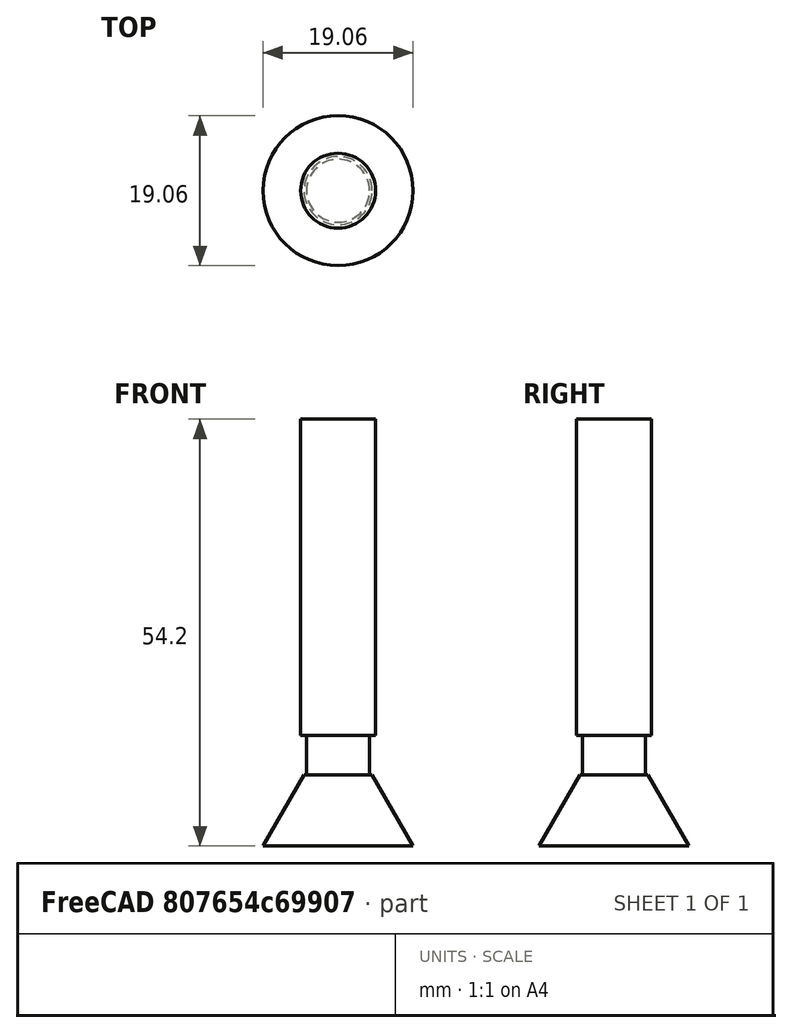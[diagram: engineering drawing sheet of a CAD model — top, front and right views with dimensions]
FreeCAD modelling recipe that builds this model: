
FCSTD DOCUMENT  (FreeCAD 0.21R32331 +3 (Git))
Label: dovetail
License: Creative Commons Attribution 4.0
LicenseURL: https://creativecommons.org/licenses/by/4.0/
objects: Sketcher::SketchObject×1, PartDesign::Revolution×1, App::FeaturePython×1, PartDesign::Body×1
note: 4 computed .brp shape members not serialized (recipe doc carries the construction recipe); baked Part::Feature solids carry a one-line shape summary decoded from their .brp

FEATURE [Sketcher::SketchObject] Sketch
  FullyConstrained = true
  MapMode = 5
  Placement = pos=(0,0,0) rot=(1,0,0;1.5708rad)
  Support = -> [XZ_Plane]
  expr: Constraints[13] = <<Attributes>>.ShankDiameter
  expr: Constraints[14] = <<Attributes>>.CuttingEdgeHeight
  expr: Constraints[21] = <<Attributes>>.CuttingEdgeAngle
  expr: Constraints[28] = <<Attributes>>.NeckHeight
  expr: Constraints[31] = <<Attributes>>.NeckDiameter
  expr: Constraints[7] = <<Attributes>>.Diameter
  expr: Constraints[8] = <<Attributes>>.Length
  sketch-geometry (13):
    g0: LineSegment StartX=0 StartY=54.2 StartZ=0 EndX=0 EndY=0 EndZ=0
    g1: LineSegment StartX=0 StartY=0 StartZ=0 EndX=9.525 EndY=0 EndZ=0
    g2: LineSegment StartX=9.525 StartY=0 StartZ=0 EndX=4.32885 EndY=9 EndZ=0
    g3: LineSegment StartX=4.7625 StartY=54.2 StartZ=0 EndX=0 EndY=54.2 EndZ=0
    g4: LineSegment StartX=9.525 StartY=0 StartZ=0 EndX=-9.525 EndY=0 EndZ=0
    g5: LineSegment StartX=4.7625 StartY=54.2 StartZ=0 EndX=4.7625 EndY=14 EndZ=0
    g6: LineSegment StartX=-4.7625 StartY=54.2 StartZ=0 EndX=4.7625 EndY=54.2 EndZ=0
    g7: LineSegment StartX=4.32885 StartY=9 StartZ=0 EndX=-4.32885 EndY=9 EndZ=0
    g8: LineSegment StartX=-9.525 StartY=0 StartZ=0 EndX=-4.32885 EndY=9 EndZ=0
    g9: LineSegment StartX=4.32885 StartY=9 StartZ=0 EndX=4 EndY=9 EndZ=0
    g10: LineSegment StartX=4 StartY=9 StartZ=0 EndX=4 EndY=14 EndZ=0
    g11: LineSegment StartX=4 StartY=14 StartZ=0 EndX=4.7625 EndY=14 EndZ=0
    g12: GeomPoint X=-4 Y=9 Z=0
  constraints (32):
    c: Vertical(g0)
    c: Coincident(g0,g1)
    c: Horizontal(g1)
    c: Coincident(g1,g2)
    c: Horizontal(g3)
    c: Coincident(g4,g1)
    c: Symmetric(g1,g4,g0)
    c: DistanceX(g4,g4) = 19.05
    c: DistanceY(g2,g3) = 54.2
    c: Vertical(g5)
    c: Coincident(g3,g5)
    c: Symmetric(g6,g6,g0)
    c: Coincident(g6,g3)
    c: DistanceX(g6,g6) = 9.525
    c: DistanceY(g2) = 9
    c: Coincident(g0,g-1)
    c: Coincident(g0,g3)
    c: Coincident(g7,g2)
    c: Symmetric(g7,g2,g0)
    c: Coincident(g8,g4)
    c: Coincident(g8,g7)
    c: Angle(g2,g1) = 1.0472
    c: Coincident(g2,g9)
    c: PointOnObject(g9,g7)
    c: Coincident(g9,g10)
    c: Vertical(g10)
    c: Coincident(g10,g11)
    c: Horizontal(g11)
    c: DistanceY(g10,g10) = 5
    c: Coincident(g11,g5)
    c: Symmetric(g12,g9,g0)
    c: DistanceX(g12,g9) = 8
FEATURE [PartDesign::Revolution] Revolution
  AllowMultiFace = false
  Angle = 360
  Axis = (0,-2e-16,1)
  Base = (0,0,0)
  Placement = pos=(0,0,0) rot=(1,0,0;1.5708rad)
  Profile = -> Sketch
  ReferenceAxis = -> Sketch [V_Axis]
  Reversed = true
FEATURE [App::FeaturePython] PropertyBag  label="Attributes"  # WARN: FeaturePython — macro-defined, semantics opaque (R4)
  Chipload = 0
  CustomPropertyGroups = Attributes | Shape
  CuttingEdgeAngle = 60
  CuttingEdgeHeight = 9
  Diameter = 19.05
  Flutes = 8
  Length = 54.2
  Material = 0
  NeckDiameter = 8
  NeckHeight = 5
  ShankDiameter = 9.525
  TipDiameter = 5
  expr: Diameter = 19.05
FEATURE [PartDesign::Body] Body  label="Dovetail Cutter"
  Group = -> [Sketch,Revolution,PropertyBag]
  Origin = -> Origin
  Tip = -> Revolution
